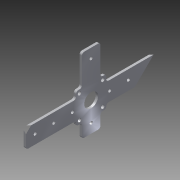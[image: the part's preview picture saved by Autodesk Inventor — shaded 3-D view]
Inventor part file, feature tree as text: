
AUTODESK INVENTOR PART (.ipt)
format: ipt  version: 2014 (Build 180170000, 170)  size: 163,328 bytes
history: native  units: in
note: dims shown in document units (in); Inventor stores cm internally (conversion verified against a paired STEP export)
features: extrude x2, sketch x2
ambient origin geometry x8: Origin, YZ Plane, XZ Plane, XY Plane, X Axis, Y Axis, Z Axis, Center Point
bodies: Solid1 (feature_tree)
feature tree (4):
  extrude  "Extrusion1"  Depth=4.0in
  extrude  "Extrusion2"  Depth=1.625in
  sketch  "Sketch1"  dims[d0=1.0in d1=4.0in]
  sketch  "Sketch2"  dims[d2=1.625in d3=1.625in d5=0.164in d6=0.164in d7=1.25in d8=1.25in d10=0.1875in d11=0.5in d12=0.5in d13=0.5in d15=0.188in d16=0.7874in d18=1.25in d19=0.7874in d21=1.25in d24=0.75in d25=0.8125in d26=0.8125in d27=0.125in d28=0.0in d29=2.44in d30=0.1875in d31=0.5in d32=1.0in d33=1.0in d34=3.0in d35=1.0in d36=3.0in d37=1.625in d38=0.1875in d39=0.8125in d40=1.625in d41=0.1875in d42=0.8125in d44=0.164in d45=0.164in d46=0.5in d47=0.5in d48=1.1811in d50=1.0in d51=0.3937in d53=1.0in d55=0.5in d56=0.5in d57=1.1811in d59=1.0in d60=0.3937in d62=1.0in d64=0.375in d65=0.375in d66=0.375in d67=0.375in d68=1.0in d69=0.0in]
